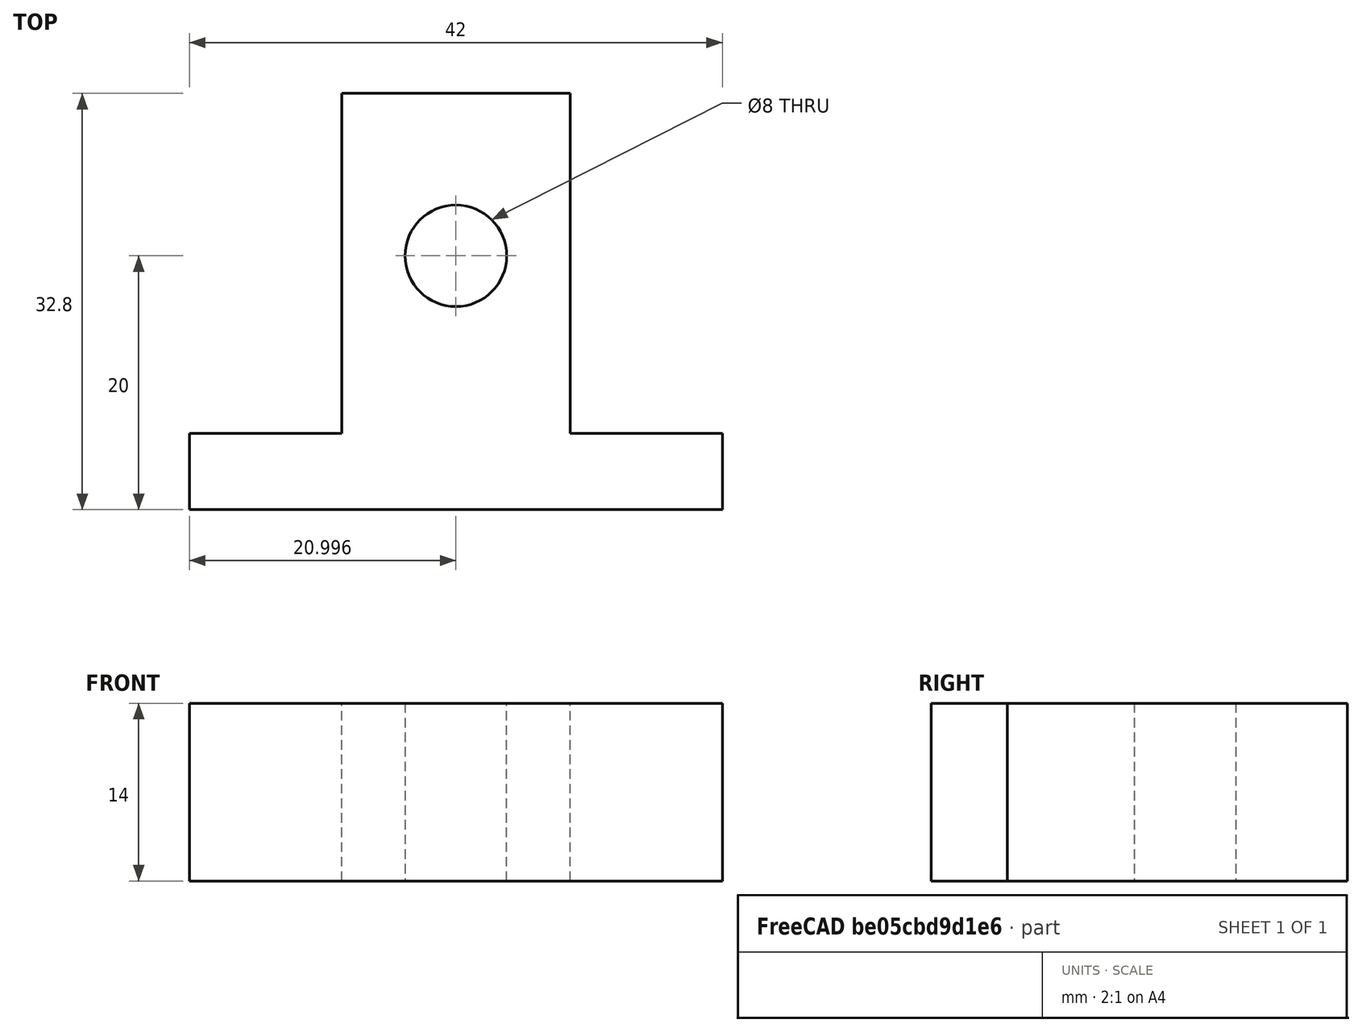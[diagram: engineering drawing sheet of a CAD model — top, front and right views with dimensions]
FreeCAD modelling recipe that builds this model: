
FCSTD DOCUMENT  (FreeCAD 0.14R3700 (Git))
Label: 8mm_rail_support_guideTslot
License: CC-BY 3.0
LicenseURL: http://creativecommons.org/licenses/by/3.0/
objects: Sketcher::SketchObject×2, App::MeasureDistance×2, PartDesign::Pad×1
note: 4 computed .brp shape members not serialized (recipe doc carries the construction recipe); baked Part::Feature solids carry a one-line shape summary decoded from their .brp

FEATURE [Sketcher::SketchObject] Sketch
  sketch-geometry (9):
    g0: LineSegment StartX=-21 StartY=0 StartZ=0 EndX=21 EndY=0 EndZ=0
    g1: LineSegment StartX=21 StartY=0 StartZ=0 EndX=21 EndY=6 EndZ=0
    g2: LineSegment StartX=21 StartY=6 StartZ=0 EndX=9 EndY=6 EndZ=0
    g3: LineSegment StartX=9 StartY=6 StartZ=0 EndX=9 EndY=32.8 EndZ=0
    g4: LineSegment StartX=9 StartY=32.8 StartZ=0 EndX=-9 EndY=32.8 EndZ=0
    g5: LineSegment StartX=-9 StartY=32.8 StartZ=0 EndX=-9 EndY=6 EndZ=0
    g6: LineSegment StartX=-9 StartY=6 StartZ=0 EndX=-21 EndY=6 EndZ=0
    g7: LineSegment StartX=-21 StartY=6 StartZ=0 EndX=-21 EndY=0 EndZ=0
    g8: Circle CenterX=-0.00411 CenterY=20 CenterZ=0 NormalX=0 NormalY=0 NormalZ=1 Radius=4
  constraints (27):
    c: PointOnObject(g0,g-1)
    c: PointOnObject(g0,g-1)
    c: Coincident(g1,g0)
    c: Vertical(g1)
    c: Coincident(g2,g1)
    c: Horizontal(g2)
    c: Coincident(g3,g2)
    c: Vertical(g3)
    c: Coincident(g4,g3)
    c: Horizontal(g4)
    c: Coincident(g5,g4)
    c: Vertical(g5)
    c: Coincident(g6,g5)
    c: Horizontal(g6)
    c: Coincident(g7,g6)
    c: Coincident(g7,g0)
    c: Vertical(g7)
    c: Distance(g0) = 42
    c: Distance(g7) = 6
    c: Equal(g7,g1)
    c: Distance(g4) = 18
    c: Distance(g6) = 12
    c: Equal(g6,g2)
    c: Symmetric(g0,g0,g-1)
    c: Distance(g3) = 26.8
    c: Radius(g8) = 4
    c: Distance(g8,g0) = 20
FEATURE [PartDesign::Pad] Pad  label="8mm_rail_support_guide"
  Length = 14
  Length2 = 10
  Sketch = -> Sketch
  Type = 0
FEATURE [App::MeasureDistance] Distance  label="Distance: 17.968"
  Distance = 17.9682
  P1 = (-8.96815,32.8,0)
  P2 = (9,32.8,0)
FEATURE [App::MeasureDistance] Distance001  label="Distance: 7.969"
  Distance = 7.96884
  P1 = (3.99589,20,0)
  P2 = (-3.97257,19.9221,0)
FEATURE [Sketcher::SketchObject] Sketch002
  Placement = pos=(0,6,0) rot=(0,0.707107,0.707107;3.14159rad)
  Support = -> Pad [Face3]
  sketch-geometry (2):
    g0: Circle [constr] CenterX=-15 CenterY=6.16537 CenterZ=0 NormalX=0 NormalY=0 NormalZ=1 Radius=3.25
    g1: Circle CenterX=15 CenterY=6.18305 CenterZ=0 NormalX=0 NormalY=0 NormalZ=1 Radius=3.25
  constraints (4):
    c: Radius(g0) = 3.25
    c: Equal(g1,g0)
    c: DistanceX(g0,g1) = 30
    c: DistanceX(g-1,g0) = -15
